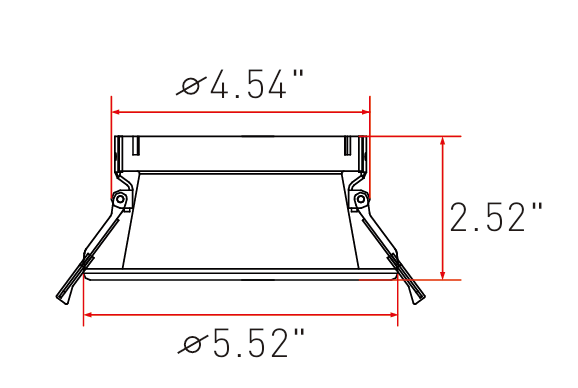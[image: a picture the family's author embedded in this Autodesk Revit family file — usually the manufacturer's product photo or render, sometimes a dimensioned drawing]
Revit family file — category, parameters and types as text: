
# Revit family: Alcon-14123-4R-WW-Revit-Family
name_source: partatom
category: Lighting Fixtures
units: mm (PartAtom-declared; Revit-internal decimal feet)

## family parameters
Always vertical = Yes
Cut with Voids When Loaded = No
Host = Ceiling
Light Source = Yes
OmniClass Number = 23.80.70.11
OmniClass Title = Luminaries for Internal Lighting
Part Type = Normal
Room Calculation Point = No
Round Connector Dimension = Use Diameter
Shared = No

## types (1)
- Type 1
    Color Filter = 16777215
    Default Elevation = 0' - 0"
    Dimming Lamp Color Temperature Shift = <None>
    Housing = <By Category>
    Light Source Symbol Length = 10' - 0"
    LightSource = <By Category>
    Link To Product Page = https://www.alconlighting.com
    Manufacturer = Alcon Light
    Product Identity = Alcon Lighting 14123-4R-WW
    Spot Beam Angle = 30.00°
    Spot Field Angle = 90.00°
    Tilt Angle = 60.00°

## geometry (parser evidence)
native form markers: Sweep x2
no freeform markers — native parametric forms only
